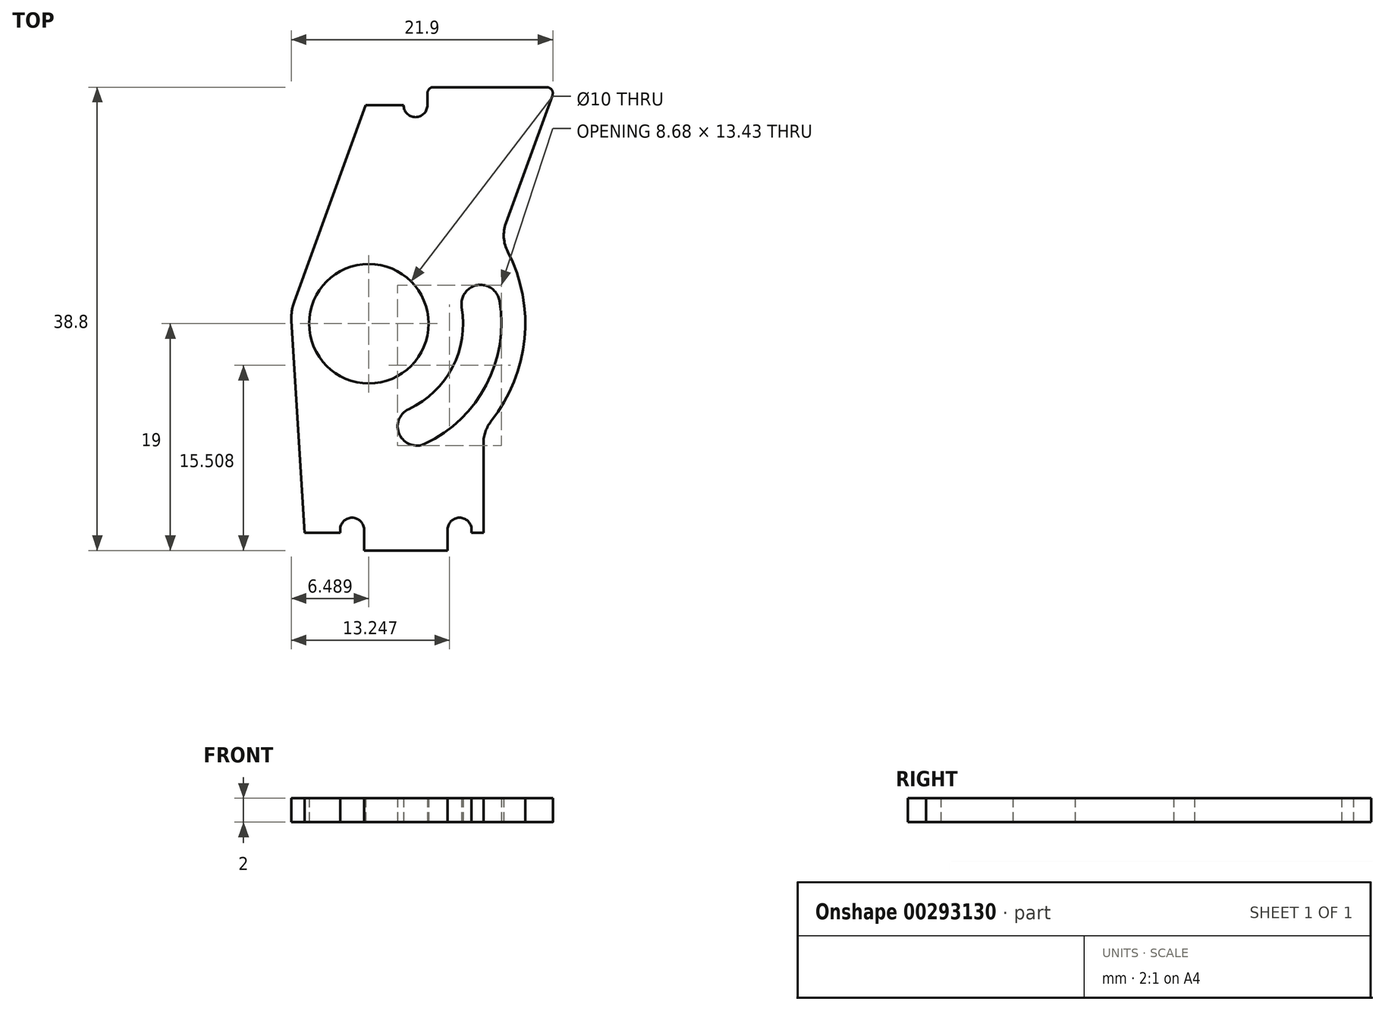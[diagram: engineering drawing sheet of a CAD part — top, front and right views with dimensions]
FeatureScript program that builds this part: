
annotation { "Feature Type Name" : "Feature", "Feature Type Description" : "" }
export const myFeature = defineFeature(function(context is Context, id is Id, definition is map)
    precondition{}
    {
        {
            var Q0;
            Q0=qCreatedBy(makeId("Top.planeOp"),FACE);
            var sketch = newSketch(context, id + "F0", { "sketchPlane" : qUnion([Q0])});
            skLineSegment(sketch, "E0", {"start": v(7.02, 8.02) * mm, "end": v(10.91, 18.73) * mm});
            skArc(sketch, "E1", {"start": v(10.91, 18.73) * mm, "mid": v(10.85, 19.19) * mm, "end": v(10.45, 19.4) * mm});
            skLineSegment(sketch, "E2", {"start": v(10.45, 19.4) * mm, "end": v(0.95, 19.4) * mm});
            skArc(sketch, "E3", {"start": v(0.95, 19.4) * mm, "mid": v(0.6, 19.25) * mm, "end": v(0.45, 18.9) * mm});
            skLineSegment(sketch, "E4", {"start": v(0.45, 18.9) * mm, "end": v(0.45, 17.9) * mm});
            skArc(sketch, "E5", {"start": v(-1.55, 17.9) * mm, "mid": v(-0.55, 16.9) * mm, "end": v(0.45, 17.9) * mm});
            skLineSegment(sketch, "E6", {"start": v(-1.55, 17.9) * mm, "end": v(-4.72, 17.9) * mm});
            skLineSegment(sketch, "E7", {"start": v(-4.72, 17.9) * mm, "end": v(-10.7, 1.45) * mm});
            skArc(sketch, "E8", {"start": v(-10.7, 1.45) * mm, "mid": v(-10.9, 0.66) * mm, "end": v(-10.94, -0.16) * mm});
            skLineSegment(sketch, "E9", {"start": v(-10.94, -0.16) * mm, "end": v(-9.84, -17.9) * mm});
            skLineSegment(sketch, "E10", {"start": v(-9.84, -17.9) * mm, "end": v(-6.86, -17.9) * mm});
            skLineSegment(sketch, "E11", {"start": v(-6.86, -17.9) * mm, "end": v(-6.86, -17.65) * mm});
            skArc(sketch, "E12", {"start": v(-4.86, -17.65) * mm, "mid": v(-5.86, -16.65) * mm, "end": v(-6.86, -17.65) * mm});
            skLineSegment(sketch, "E13", {"start": v(-4.86, -17.65) * mm, "end": v(-4.86, -19.4) * mm});
            skLineSegment(sketch, "E14", {"start": v(-4.86, -19.4) * mm, "end": v(2.14, -19.4) * mm});
            skLineSegment(sketch, "E15", {"start": v(2.14, -19.4) * mm, "end": v(2.14, -17.65) * mm});
            skArc(sketch, "E16", {"start": v(4.14, -17.65) * mm, "mid": v(3.14, -16.65) * mm, "end": v(2.14, -17.65) * mm});
            skLineSegment(sketch, "E17", {"start": v(4.14, -17.65) * mm, "end": v(4.14, -17.9) * mm});
            skLineSegment(sketch, "E18", {"start": v(4.14, -17.9) * mm, "end": v(5.14, -17.9) * mm});
            skLineSegment(sketch, "E19", {"start": v(5.14, -17.9) * mm, "end": v(5.14, -10.42) * mm});
            skArc(sketch, "E20", {"start": v(5.8, -8.56) * mm, "mid": v(5.3, -9.43) * mm, "end": v(5.14, -10.42) * mm});
            skArc(sketch, "E21", {"start": v(5.8, -8.56) * mm, "mid": v(8.58, -1.67) * mm, "end": v(7.17, 5.62) * mm});
            skArc(sketch, "E22", {"start": v(7.02, 8.02) * mm, "mid": v(6.84, 6.8) * mm, "end": v(7.17, 5.62) * mm});
            skCircle(sketch, "E23", {"center": v(-4.46, -0.4) * mm, "radius": 5 * mm});
            skArc(sketch, "E24", {"start": v(-1.12, -7.56) * mm, "mid": v(2.55, -4.05) * mm, "end": v(3.32, 0.97) * mm});
            skArc(sketch, "E25", {"start": v(6.47, 1.53) * mm, "mid": v(4.62, 2.83) * mm, "end": v(3.32, 0.97) * mm});
            skArc(sketch, "E26", {"start": v(0.23, -10.46) * mm, "mid": v(5.38, -5.53) * mm, "end": v(6.47, 1.53) * mm});
            skArc(sketch, "E27", {"start": v(-1.12, -7.56) * mm, "mid": v(-1.9, -9.69) * mm, "end": v(0.23, -10.46) * mm});
            skSolve(sketch);
        }
        {
            var Q0;
            Q0 = qSketchRegion(id + "F0", true);
            extrude(context, id + "F1", {"entities" : qUnion([Q0]), "depth" : 2 * mm});
        }
    });
